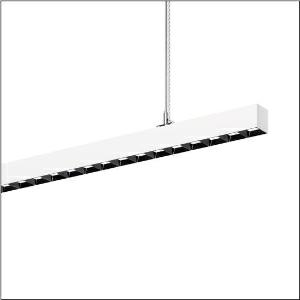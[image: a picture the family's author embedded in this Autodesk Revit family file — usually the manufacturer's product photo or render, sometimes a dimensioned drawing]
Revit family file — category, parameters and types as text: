
# Revit family: silica_r__21_51mx31tat7w_6f20
name_source: partatom
category: Lighting Fixtures
units: mm (PartAtom-declared; Revit-internal decimal feet)

## family parameters
Cut with Voids When Loaded = No
Host = Face
Light Source = No
Part Type = Normal
Room Calculation Point = No
Round Connector Dimension = Use Diameter
Shared = No

## types (1)
- --- (1 x LED, 6220 lm, 53.5 W, 6500K)
    Apparent Load = 54 VA
    CIE Flux Codes = 85 99 100 60 100
    Color Rendering = 80
    Color Temperature = 6500K
    Default Elevation = 1800 mm
    Description = Silica® 21, office luminaire, primary light control with darklight reflector, of PMMA, black, CAT 2 (L<= 3000cd/m²), light emission: direct/indirect distribution, primary light characteristic: symmetric, installation type: suspended mounting, LED, rated luminous flux: 6.220lm, luminous efficacy: 111lm/W, light colour: 8tw, colour temperature: 2700..6500K, control gear: ECG DALI, with terminal, 3+2-pole, max. 2.5mm², mains connection: 220..240V, AC, 50/60Hz, rated input power: 56.2W, luminaire housing, of aluminium, traffic white (RAL 9016), length: 1.204mm, width: 53mm, height: 53mm, protection rating (complete): IP20, insulation class (complete): insulation class I (protective earthing), certification: CE, permissible operating ambient temperature: 0..+35°C, standard: EN 50419, packaging unit: 1 piece
    Height = 53 mm
    Lamp = 1 x LED
    Lamp Light Flux = 6220 lm
    Lamp Power = 53.5 W
    Lamp count = 1
    Length = 1204 mm
    Luminous efficacy = 116 lm/W
    Manufacturer = Siteco
    ModVariant = No
    Model = 51MX31TAT7W
    Mounting Place = Ceiling
    Mounting Type = Pendant
    Number of Poles = 1
    OnlyDefault = Yes
    Power Factor = 1
    Product Name = Silica® 21
    Product group = office luminaire | ceiling pendant
    ProductGroupID = 902
    Protection Class = Protection class I
    Protection Degree = IP 20
    RLX_Detail_Level = 1
    RLX_Emergency_Light_Flux = 0 lm
    RLX_Emergency_Type = 0
    RLX_Emergency_Type_DB = No
    RlxData = <blob elided: 40493 chars, md5=39916108>
    Socket = socket
    Standby Power = 0 W
    System Light Flux = 6220 lm
    System Power = 54 W
    Type Comments = individual setting
    Type Image = l_1297801.jpg
    URL = http://relux.com
    VarID = @adj_071233
    Voltage = 0 V
    Weight = 0.00 kg
    Width = 53 mm

## geometry (parser evidence)
native form markers: Blend x4, Sweep x14
no freeform markers — native parametric forms only
